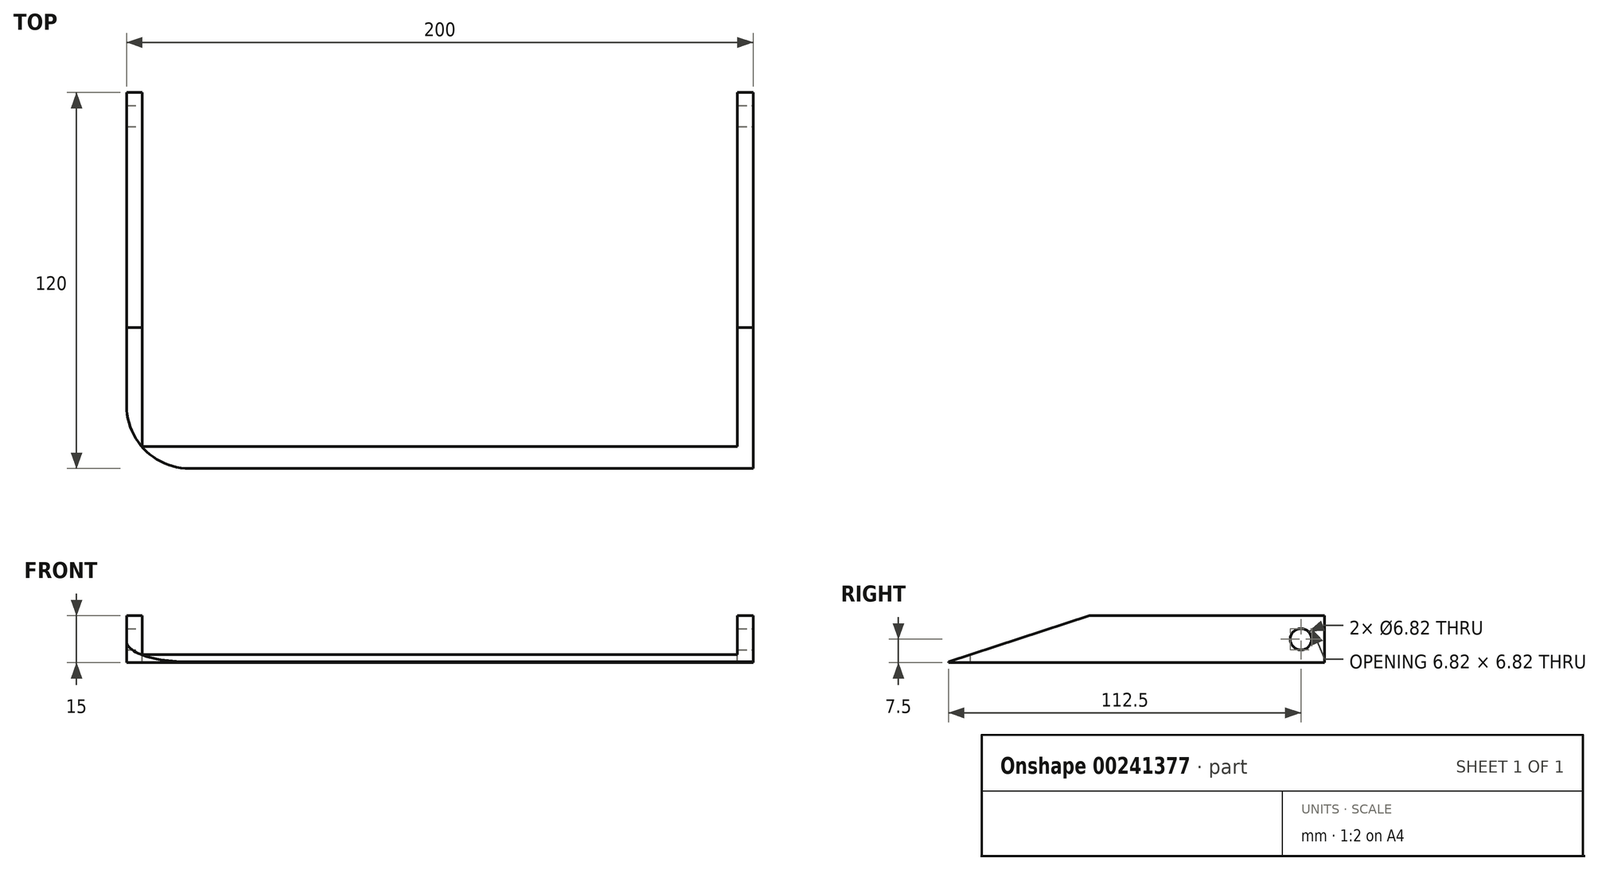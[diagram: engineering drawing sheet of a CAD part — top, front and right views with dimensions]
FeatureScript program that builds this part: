
annotation { "Feature Type Name" : "Feature", "Feature Type Description" : "" }
export const myFeature = defineFeature(function(context is Context, id is Id, definition is map)
    precondition{}
    {
        {
            var Q0;
            Q0=qCreatedBy(makeId("Top.planeOp"),FACE);
            var sketch = newSketch(context, id + "F0", { "sketchPlane" : qUnion([Q0])});
            skLineSegment(sketch, "E0.bottom", {"start": v(-100, 60) * mm, "end": v(100, 60) * mm});
            skLineSegment(sketch, "E0.top", {"start": v(-100, -60) * mm, "end": v(100, -60) * mm});
            skLineSegment(sketch, "E0.left", {"start": v(-100, 60) * mm, "end": v(-100, -60) * mm});
            skLineSegment(sketch, "E0.right", {"start": v(100, 60) * mm, "end": v(100, -60) * mm});
            skPoint(sketch, "E0.middle", {"position": v(0, 0) * mm});
            skSolve(sketch);
        }
        {
            var Q0;
            Q0 = qSketchRegion(id + "F0", true);
            extrude(context, id + "F1", {"entities" : qUnion([Q0]), "depth" : 15 * mm});
        }
        {
            var Q0;
            Q0=makeQuery(id+"F1.opExtrude","SWEPT_FACE",FACE,{"disambiguationData":[OSD([sQuery(id+"F0.wireOp",EDGE,"E0.right")])]});
            var sketch = newSketch(context, id + "F2", { "sketchPlane" : qUnion([Q0])});
            skCircle(sketch, "E1", {"center": v(52.5, 7.5) * mm, "radius": 3.41 * mm});
            skPoint(sketch, "E1.centerSnap0", {"position": v(60, 7.5) * mm});
            skSolve(sketch);
        }
        {
            var Q0;
            Q0 = qSketchRegion(id + "F2", true);
            extrude(context, id + "F3", {"entities" : qUnion([Q0]), "operationType" : NewBodyOperationType.REMOVE, "endBound" : BoundingType.THROUGH_ALL, "oppositeDirection" : true, "depth" : 25 * mm});
        }
        {
            var Q0;
            Q0=makeQuery(id+"F1.opExtrude","CAP_EDGE",EDGE,{"disambiguationData":[OSD([sQuery(id+"F0.wireOp",EDGE,"E0.top")])],"isStart":false});
            chamfer(context, id + "F4", {"entities" : qUnion([Q0]), "chamferType" : ChamferType.TWO_OFFSETS, "width1" : 45 * mm, "oppositeDirection" : false, "width2" : 14.75 * mm, "tangentPropagation" : true});
        }
        {
            var Q0;
            Q0=makeQuery(id+"F1.opExtrude","SWEPT_EDGE",EDGE,{"disambiguationData":[OSD([sQuery(id+"F0.wireOp",EDGE,"E0.top"),sQuery(id+"F0.wireOp",EDGE,"E0.left")])]});
            fillet(context, id + "F5", {"entities" : qUnion([Q0]), "radius" : 20 * mm, "tangentPropagation" : true, "allowEdgeOverflow" : false});
        }
        {
            var Q0;
            Q0=makeQuery(id+"F1.opExtrude","CAP_FACE",FACE,{"disambiguationData":[OSD([sQuery(id+"F0.wireOp",EDGE,"E0.bottom"),sQuery(id+"F0.wireOp",EDGE,"E0.top"),sQuery(id+"F0.wireOp",EDGE,"E0.left"),sQuery(id+"F0.wireOp",EDGE,"E0.right")])],"isStart":false});
            var sketch = newSketch(context, id + "F6", { "sketchPlane" : qUnion([Q0])});
            skLineSegment(sketch, "E2.bottom", {"start": v(-95, 60) * mm, "end": v(95, 60) * mm});
            skLineSegment(sketch, "E2.top", {"start": v(-95, -53) * mm, "end": v(95, -53) * mm});
            skLineSegment(sketch, "E2.left", {"start": v(-95, 60) * mm, "end": v(-95, -53) * mm});
            skLineSegment(sketch, "E2.right", {"start": v(95, 60) * mm, "end": v(95, -53) * mm});
            skSolve(sketch);
        }
        {
            var Q0;
            Q0 = qSketchRegion(id + "F6", true);
            extrude(context, id + "F7", {"entities" : qUnion([Q0]), "operationType" : NewBodyOperationType.REMOVE, "endBound" : BoundingType.THROUGH_ALL, "oppositeDirection" : true, "depth" : 25 * mm});
        }
    });
